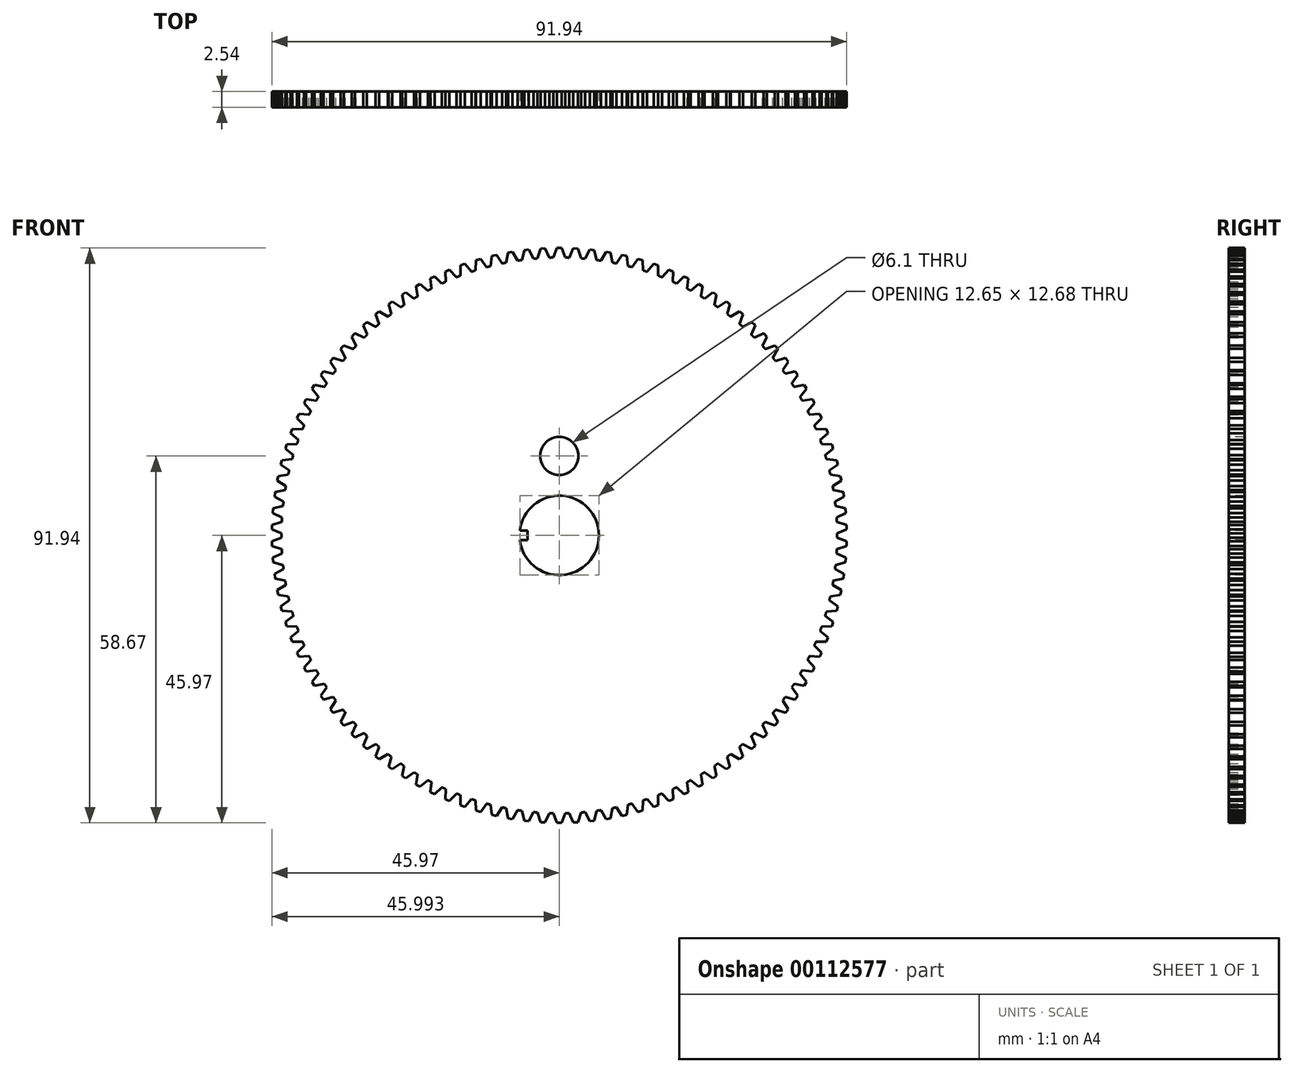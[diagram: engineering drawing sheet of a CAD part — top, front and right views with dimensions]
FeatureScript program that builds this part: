
annotation { "Feature Type Name" : "Feature", "Feature Type Description" : "" }
export const myFeature = defineFeature(function(context is Context, id is Id, definition is map)
    precondition{}
    {
        {
            var Q0;
            Q0=qCreatedBy(makeId("Front.planeOp"),FACE);
            var sketch = newSketch(context, id + "F0", { "sketchPlane" : qUnion([Q0])});
            skCircle(sketch, "E0", {"center": v(0, 0) * mm, "radius": 44.45 * mm});
            skLineSegment(sketch, "E1", {"start": v(0, 1.04) * mm, "end": v(0, 44.45) * mm});
            skLineSegment(sketch, "E2", {"start": v(0, 44.45) * mm, "end": v(0, 47) * mm});
            skLineSegment(sketch, "E3", {"start": v(0, 47) * mm, "end": v(-0.93, 44.44) * mm});
            skLineSegment(sketch, "E4", {"start": v(0, 47) * mm, "end": v(0.93, 44.44) * mm});
            skLineSegment(sketch, "E5", {"start": v(0, 45.97) * mm, "end": v(-0.37, 45.97) * mm});
            skLineSegment(sketch, "E6", {"start": v(0, 45.97) * mm, "end": v(0.37, 45.97) * mm});
            skSolve(sketch);
        }
        {
            var Q0;
            {var subQ5=sQuery(id+"F0.wireOp",EDGE,"E5");Q0=makeQuery(id+"F0.imprint","IMPRINT",FACE,{"disambiguationData":[TD([[makeQuery(id+"F0.imprint","IMPRINT",EDGE,{"derivedFrom":subQ5}),1.0]])]});}
            var Q1;
            {var subQ5=sQuery(id+"F0.wireOp",EDGE,"E6");Q1=makeQuery(id+"F0.imprint","IMPRINT",FACE,{"disambiguationData":[TD([[makeQuery(id+"F0.imprint","IMPRINT",EDGE,{"derivedFrom":subQ5}),-1.0]])]});}
            var Q2;
            {var subQ0=sQuery(id+"F0.wireOp",EDGE,"E0");var subQ1=makeQuery(id+"F0.imprint","INTERSECT",VERTEX,{"derivedFrom":[subQ0,sQuery(id+"F0.wireOp",EDGE,"E2")]});Q2=makeQuery(id+"F0.imprint","IMPRINT",FACE,{"disambiguationData":[TD([[makeQuery(id+"F0.imprint","IMPRINT",EDGE,{"disambiguationData":[TD([[subQ1,1.0]])],"derivedFrom":subQ0}),1.0]])]});}
            extrude(context, id + "F1", {"entities" : qUnion([Q0, Q1, Q2]), "depth" : 2.54 * mm});
        }
        {
            var Q0;
            Q0=makeQuery(id+"F1.opExtrude","SWEPT_BODY",BODY,{"disambiguationData":[OSD([sQuery(id+"F0.wireOp",EDGE,"E0"),sQuery(id+"F0.wireOp",EDGE,"E3"),sQuery(id+"F0.wireOp",EDGE,"E4"),sQuery(id+"F0.wireOp",EDGE,"E5"),sQuery(id+"F0.wireOp",EDGE,"E6")])]});
            var Q1;
            Q1=makeQuery(id+"F1.opExtrude","SWEPT_FACE",FACE,{"disambiguationData":[OSD([sQuery(id+"F0.wireOp",EDGE,"E4")])]});
            var Q2;
            Q2=makeQuery(id+"F1.opExtrude","SWEPT_FACE",FACE,{"disambiguationData":[OSD([sQuery(id+"F0.wireOp",EDGE,"E5"),sQuery(id+"F0.wireOp",EDGE,"E6")])]});
            var Q3;
            Q3=makeQuery(id+"F1.opExtrude","SWEPT_FACE",FACE,{"disambiguationData":[OSD([sQuery(id+"F0.wireOp",EDGE,"E3")])]});
            var Q4;
            Q4=makeQuery(id+"F1.opExtrude","SWEPT_FACE",FACE,{"disambiguationData":[OSD([sQuery(id+"F0.wireOp",EDGE,"E0")])]});
            circularPattern(context, id + "F2", {"patternType" : PatternType.FACE, "operationType" : NewBodyOperationType.ADD, "faces" : qUnion([Q1, Q2, Q3]), "axis" : qUnion([Q4]), "angle" : 360 * degree, "instanceCount" : 110, "equalSpace" : true});
        }
        {
            var Q0;
            Q0=makeQuery(id+"F1.opExtrude","CAP_FACE",FACE,{"disambiguationData":[OSD([sQuery(id+"F0.wireOp",EDGE,"E0"),sQuery(id+"F0.wireOp",EDGE,"E3"),sQuery(id+"F0.wireOp",EDGE,"E4"),sQuery(id+"F0.wireOp",EDGE,"E5"),sQuery(id+"F0.wireOp",EDGE,"E6")])],"isStart":false});
            var sketch = newSketch(context, id + "F3", { "sketchPlane" : qUnion([Q0])});
            skCircle(sketch, "E7", {"center": v(0, 0) * mm, "radius": 6.35 * mm});
            skLineSegment(sketch, "E8", {"start": v(0, 0) * mm, "end": v(0, 12.7) * mm});
            skCircle(sketch, "E9", {"center": v(0, 12.7) * mm, "radius": 3.05 * mm});
            skSolve(sketch);
        }
        {
            var Q0;
            Q0=makeQuery(id+"F3.imprint","IMPRINT",FACE,{"disambiguationData":[TD([[makeQuery(id+"F3.imprint","IMPRINT",EDGE,{"derivedFrom":sQuery(id+"F3.wireOp",EDGE,"E7")}),1.0]])]});
            var Q1;
            Q1=makeQuery(id+"F3.imprint","IMPRINT",FACE,{"disambiguationData":[TD([[makeQuery(id+"F3.imprint","IMPRINT",EDGE,{"derivedFrom":sQuery(id+"F3.wireOp",EDGE,"E9")}),1.0]])]});
            extrude(context, id + "F4", {"entities" : qUnion([Q0, Q1]), "operationType" : NewBodyOperationType.REMOVE, "oppositeDirection" : true, "depth" : 25.4 * mm});
        }
        {
            var Q0;
            Q0=makeQuery(id+"F1.opExtrude","CAP_FACE",FACE,{"disambiguationData":[OSD([sQuery(id+"F0.wireOp",EDGE,"E0"),sQuery(id+"F0.wireOp",EDGE,"E3"),sQuery(id+"F0.wireOp",EDGE,"E4"),sQuery(id+"F0.wireOp",EDGE,"E5"),sQuery(id+"F0.wireOp",EDGE,"E6")])],"isStart":false});
            var sketch = newSketch(context, id + "F5", { "sketchPlane" : qUnion([Q0])});
            skLineSegment(sketch, "E10", {"start": v(0, 0) * mm, "end": v(-6.35, 0) * mm});
            skLineSegment(sketch, "E11", {"start": v(-6.35, 0) * mm, "end": v(-6.35, 0.76) * mm});
            skLineSegment(sketch, "E12", {"start": v(-6.35, 0) * mm, "end": v(-6.35, -0.76) * mm});
            skLineSegment(sketch, "E13", {"start": v(-6.35, -0.76) * mm, "end": v(-5.08, -0.76) * mm});
            skLineSegment(sketch, "E14", {"start": v(-5.08, -0.76) * mm, "end": v(-5.08, 0) * mm});
            skLineSegment(sketch, "E15", {"start": v(-5.08, 0) * mm, "end": v(-5.08, 0.76) * mm});
            skLineSegment(sketch, "E16", {"start": v(-5.08, 0.76) * mm, "end": v(-6.35, 0.76) * mm});
            skSolve(sketch);
        }
        {
            var Q0;
            {var subQ3=sQuery(id+"F5.wireOp",EDGE,"E15");Q0=makeQuery(id+"F5.imprint","IMPRINT",FACE,{"disambiguationData":[TD([[makeQuery(id+"F5.imprint","IMPRINT",EDGE,{"derivedFrom":subQ3}),1.0]])]});}
            var Q1;
            {var subQ3=sQuery(id+"F5.wireOp",EDGE,"E14");Q1=makeQuery(id+"F5.imprint","IMPRINT",FACE,{"disambiguationData":[TD([[makeQuery(id+"F5.imprint","IMPRINT",EDGE,{"derivedFrom":subQ3}),1.0]])]});}
            var Q2;
            Q2=makeQuery(id+"F1.opExtrude","CAP_FACE",FACE,{"disambiguationData":[OSD([sQuery(id+"F0.wireOp",EDGE,"E0"),sQuery(id+"F0.wireOp",EDGE,"E3"),sQuery(id+"F0.wireOp",EDGE,"E4"),sQuery(id+"F0.wireOp",EDGE,"E5"),sQuery(id+"F0.wireOp",EDGE,"E6")])],"isStart":true});
            var Q3;
            Q3=makeQuery(id+"F1.opExtrude","SWEPT_BODY",BODY,{"disambiguationData":[OSD([sQuery(id+"F0.wireOp",EDGE,"E0"),sQuery(id+"F0.wireOp",EDGE,"E3"),sQuery(id+"F0.wireOp",EDGE,"E4"),sQuery(id+"F0.wireOp",EDGE,"E5"),sQuery(id+"F0.wireOp",EDGE,"E6")])]});
            extrude(context, id + "F6", {"entities" : qUnion([Q0, Q1]), "operationType" : NewBodyOperationType.ADD, "endBound" : BoundingType.UP_TO_SURFACE, "oppositeDirection" : true, "endBoundEntityFace" : qUnion([Q2]), "endBoundEntityBody" : qUnion([Q3]), "depth" : 25.4 * mm});
        }
    });
